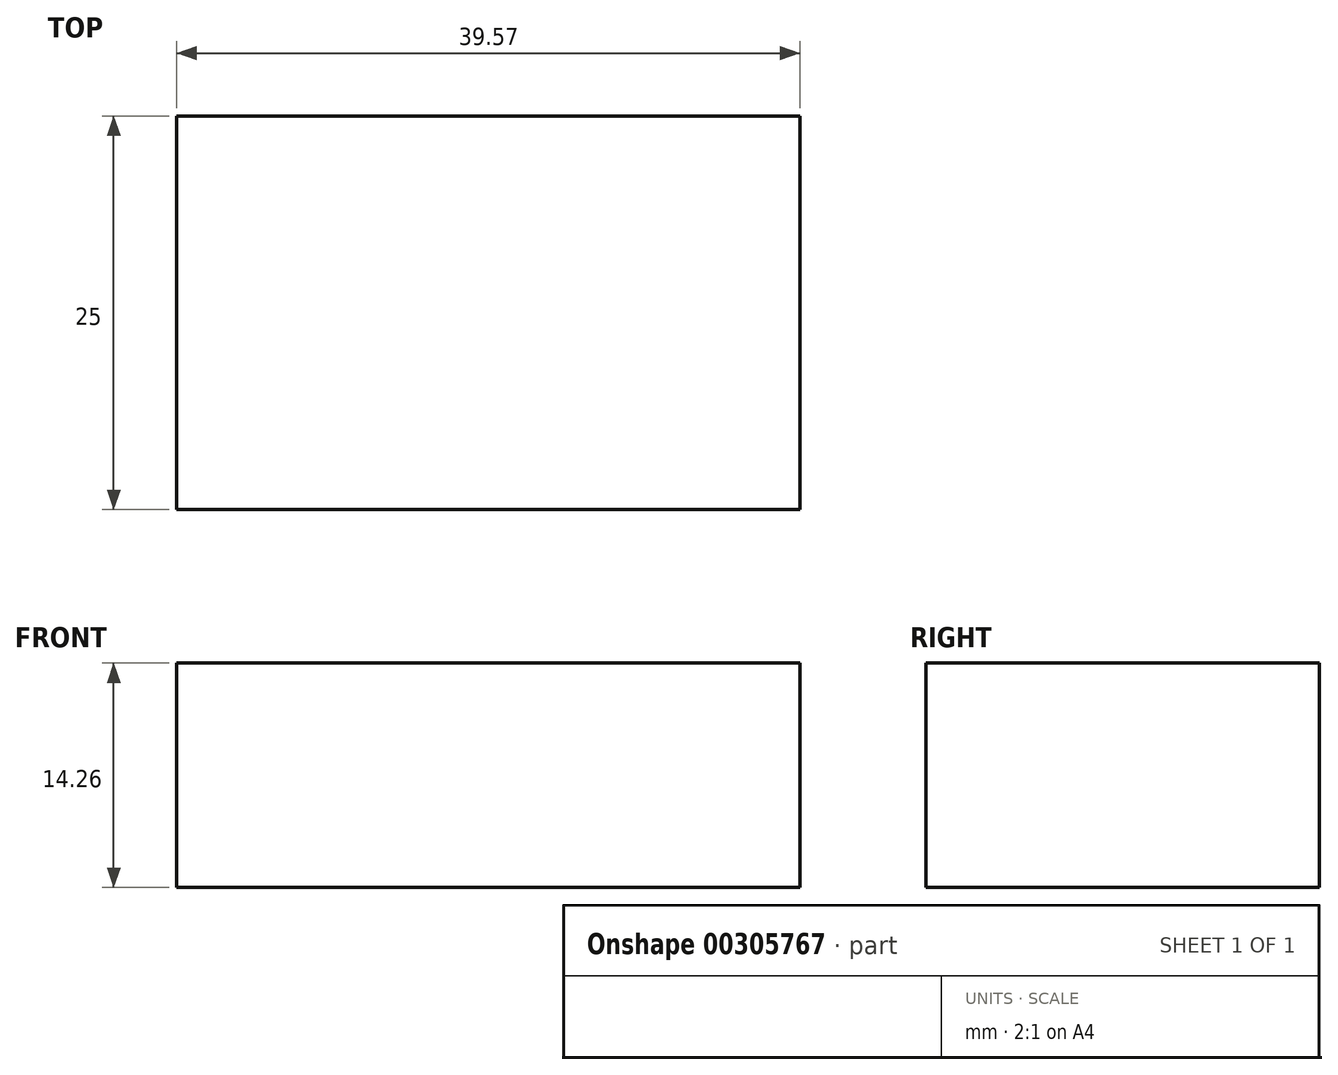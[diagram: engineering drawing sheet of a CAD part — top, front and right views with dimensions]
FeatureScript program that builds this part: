
annotation { "Feature Type Name" : "Feature", "Feature Type Description" : "" }
export const myFeature = defineFeature(function(context is Context, id is Id, definition is map)
    precondition{}
    {
        {
            var Q0;
            Q0=qCreatedBy(makeId("Front.planeOp"),FACE);
            var sketch = newSketch(context, id + "F0", { "sketchPlane" : qUnion([Q0])});
            skLineSegment(sketch, "E0.bottom", {"start": v(-102.88, 40.73) * mm, "end": v(-40.9, 40.73) * mm});
            skLineSegment(sketch, "E0.top", {"start": v(-102.88, -6.61) * mm, "end": v(-40.9, -6.61) * mm});
            skLineSegment(sketch, "E0.left", {"start": v(-102.88, 40.73) * mm, "end": v(-102.88, -6.61) * mm});
            skLineSegment(sketch, "E0.right", {"start": v(-40.9, 40.73) * mm, "end": v(-40.9, -6.61) * mm});
            skSolve(sketch);
        }
        {
            var Q0;
            Q0=sQuery(id+"F0.wireOp",EDGE,"E0.bottom");
            var Q1;
            Q1=sQuery(id+"F0.wireOp",EDGE,"E0.top");
            extrude(context, id + "F1", {"bodyType" : ToolBodyType.SURFACE, "surfaceEntities" : qUnion([Q0, Q1]), "depth" : 25 * mm});
        }
        {
            var Q0;
            Q0=qCreatedBy(makeId("Front.planeOp"),FACE);
            var sketch = newSketch(context, id + "F2", { "sketchPlane" : qUnion([Q0])});
            skLineSegment(sketch, "E1.bottom", {"start": v(-35.14, 76.05) * mm, "end": v(4.43, 76.05) * mm});
            skLineSegment(sketch, "E1.top", {"start": v(-35.14, 61.79) * mm, "end": v(4.43, 61.79) * mm});
            skLineSegment(sketch, "E1.left", {"start": v(-35.14, 76.05) * mm, "end": v(-35.14, 61.79) * mm});
            skLineSegment(sketch, "E1.right", {"start": v(4.43, 76.05) * mm, "end": v(4.43, 61.79) * mm});
            skSolve(sketch);
        }
        {
            var Q0;
            Q0 = qSketchRegion(id + "F2", true);
            extrude(context, id + "F3", {"entities" : qUnion([Q0]), "depth" : 25 * mm});
        }
    });
